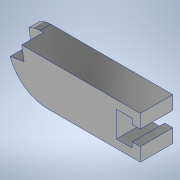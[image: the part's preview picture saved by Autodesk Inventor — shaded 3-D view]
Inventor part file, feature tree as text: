
AUTODESK INVENTOR PART (.ipt)
format: ipt  version: 2022 (Build 260153000, 153)  size: 162,816 bytes
history: native  units: mm
features: extrude x3, sketch x3, fillet x1
ambient origin geometry x8: Origin, YZ Plane, XZ Plane, XY Plane, X Axis, Y Axis, Z Axis, Center Point
bodies: Body1 (feature_tree)
feature tree (7):
  extrude  "Extrusion2"  Depth=5.8mm
  extrude  "Extrusion7"  Depth=12.0mm TaperAngle=0.0deg
  extrude  "Extrusion10"  Depth=15.6mm
  fillet  "Fillet2"  [1 undecoded]
  sketch  "Sketch5"  dims[d41=5.8mm d48=44.0mm]
  sketch  "Sketch11"  dims[d50=3.0mm d56=12.0mm d57=0.0mm]
  sketch  "Sketch14"  dims[d63=45.0mm d67=15.6mm d71=0.0mm d72=36.2mm d87=5.6mm d88=9.5mm d95=17.453293mm d96=5.0mm d97=10.0mm d98=8.0mm d99=0.0mm d107=5.5mm d108=0.0mm d109=0.0mm d110=15.0mm]
note: 1 required parameter value undecoded (feature->parameter linkage not recoverable at this tier; creation-order binding heuristic only, values carry confidence <= 0.55)
